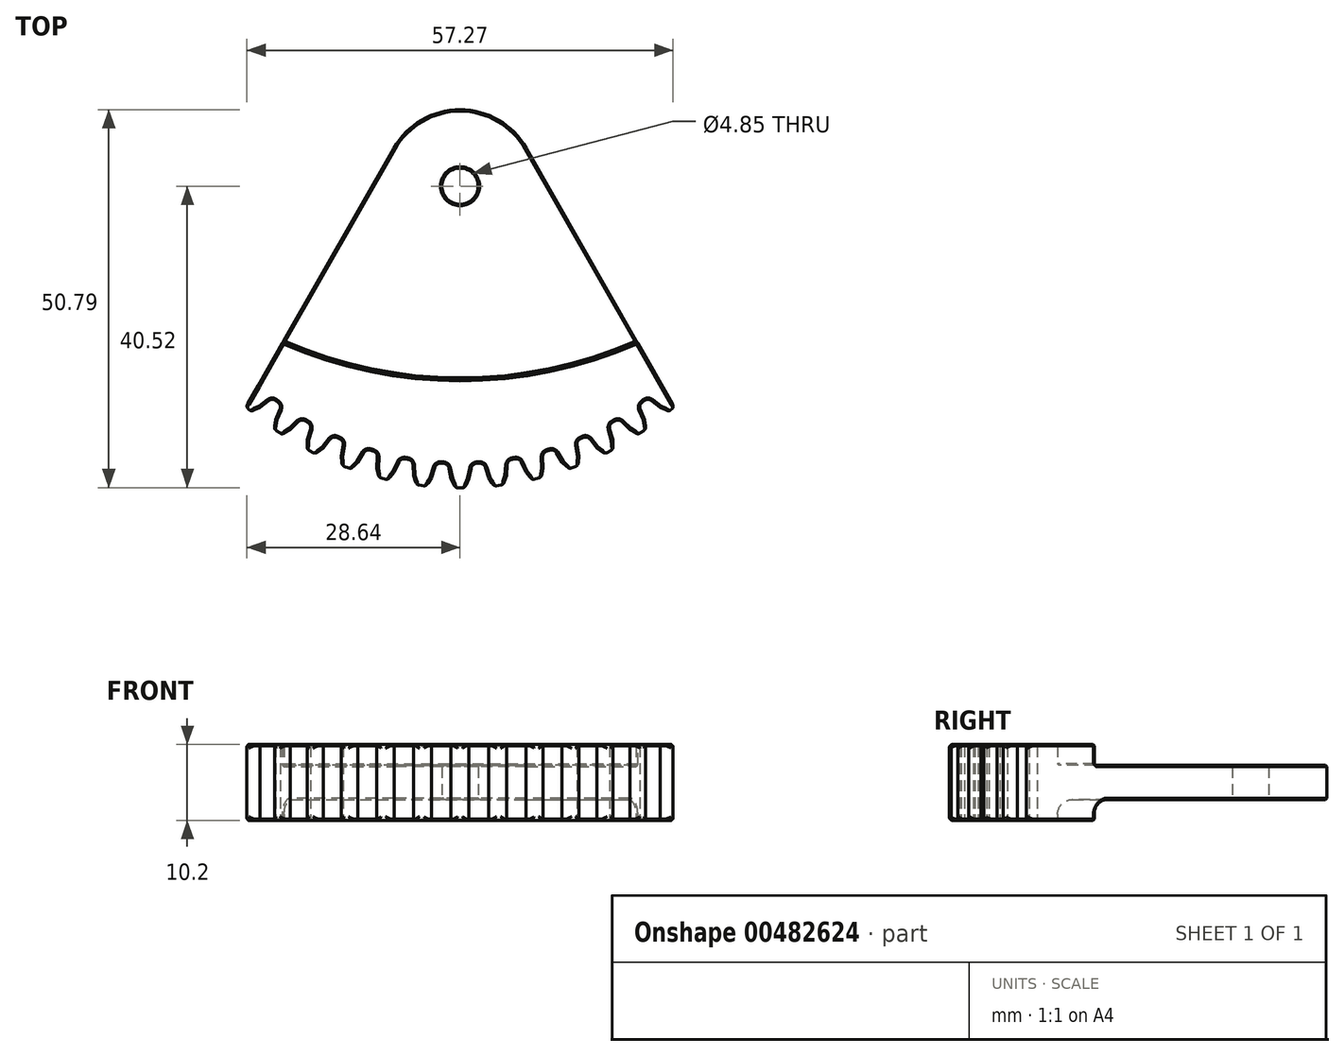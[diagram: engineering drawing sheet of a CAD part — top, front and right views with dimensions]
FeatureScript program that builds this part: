
annotation { "Feature Type Name" : "Feature", "Feature Type Description" : "" }
export const myFeature = defineFeature(function(context is Context, id is Id, definition is map)
    precondition{}
    {
        {
            var Q0;
            Q0=qCreatedBy(makeId("Top.planeOp"),FACE);
            var sketch = newSketch(context, id + "F0", { "sketchPlane" : qUnion([Q0])});
            skCircle(sketch, "E0", {"center": v(0, 0) * mm, "radius": 2.43 * mm});
            skCircle(sketch, "E1", {"center": v(0, 0) * mm, "radius": 10.27 * mm});
            skLineSegment(sketch, "E2", {"start": v(-8.92, 5.1) * mm, "end": v(-23.8, -20.96) * mm});
            skLineSegment(sketch, "E3.MirrorCS", {"start": v(8.92, 5.1) * mm, "end": v(23.8, -20.96) * mm});
            skLineSegment(sketch, "E4", {"start": v(-23.8, -20.96) * mm, "end": v(23.8, -20.96) * mm});
            skArc(sketch, "E5", {"start": v(-23.8, -20.96) * mm, "mid": v(0, -25.96) * mm, "end": v(23.8, -20.96) * mm});
            skArc(sketch, "E6", {"start": v(-27.15, -26.82) * mm, "mid": v(0, -37.32) * mm, "end": v(27.15, -26.82) * mm});
            skLineSegment(sketch, "E7", {"start": v(0, -25.96) * mm, "end": v(0, -37.32) * mm});
            skLineSegment(sketch, "E8", {"start": v(23.8, -20.96) * mm, "end": v(27.15, -26.82) * mm});
            skLineSegment(sketch, "E9", {"start": v(-23.8, -20.96) * mm, "end": v(-27.15, -26.82) * mm});
            skLineSegment(sketch, "E10", {"start": v(0, -37.32) * mm, "end": v(0, -40.52) * mm});
            skLineSegment(sketch, "E11", {"start": v(0, -40.52) * mm, "end": v(0.64, -40.52) * mm});
            skLineSegment(sketch, "E12", {"start": v(0.64, -40.52) * mm, "end": v(1.2, -39.35) * mm});
            skLineSegment(sketch, "E13", {"start": v(1.2, -39.35) * mm, "end": v(1.6, -37.28) * mm});
            skLineSegment(sketch, "E14.MirrorCS", {"start": v(-1.2, -39.35) * mm, "end": v(-1.6, -37.28) * mm});
            skLineSegment(sketch, "E15.MirrorCS", {"start": v(-0.64, -40.52) * mm, "end": v(-1.2, -39.35) * mm});
            skLineSegment(sketch, "E16.MirrorCS", {"start": v(0, -40.52) * mm, "end": v(-0.64, -40.52) * mm});
            skLineSegment(sketch, "E17.1.0", {"start": v(-3.85, -39.19) * mm, "end": v(-3.2, -37.19) * mm});
            skLineSegment(sketch, "E17.1.1", {"start": v(-6.23, -38.9) * mm, "end": v(-6.39, -36.8) * mm});
            skLineSegment(sketch, "E17.1.2", {"start": v(-5.82, -40.13) * mm, "end": v(-6.23, -38.9) * mm});
            skLineSegment(sketch, "E17.1.3", {"start": v(-5.18, -40.2) * mm, "end": v(-5.82, -40.13) * mm});
            skLineSegment(sketch, "E17.1.4", {"start": v(-5.18, -40.2) * mm, "end": v(-4.55, -40.28) * mm});
            skLineSegment(sketch, "E17.1.5", {"start": v(-4.55, -40.28) * mm, "end": v(-3.85, -39.19) * mm});
            skLineSegment(sketch, "E17.2.0", {"start": v(-8.85, -38.43) * mm, "end": v(-7.97, -36.52) * mm});
            skLineSegment(sketch, "E17.2.1", {"start": v(-11.18, -37.86) * mm, "end": v(-11.08, -35.76) * mm});
            skLineSegment(sketch, "E17.2.2", {"start": v(-10.91, -39.13) * mm, "end": v(-11.18, -37.86) * mm});
            skLineSegment(sketch, "E17.2.3", {"start": v(-10.29, -39.28) * mm, "end": v(-10.91, -39.13) * mm});
            skLineSegment(sketch, "E17.2.4", {"start": v(-10.29, -39.28) * mm, "end": v(-9.67, -39.43) * mm});
            skLineSegment(sketch, "E17.2.5", {"start": v(-9.67, -39.43) * mm, "end": v(-8.85, -38.43) * mm});
            skLineSegment(sketch, "E17.3.0", {"start": v(-13.72, -37.08) * mm, "end": v(-12.62, -35.3) * mm});
            skLineSegment(sketch, "E17.3.1", {"start": v(-15.97, -36.24) * mm, "end": v(-15.62, -34.17) * mm});
            skLineSegment(sketch, "E17.3.2", {"start": v(-15.85, -37.53) * mm, "end": v(-15.97, -36.24) * mm});
            skLineSegment(sketch, "E17.3.3", {"start": v(-15.25, -37.76) * mm, "end": v(-15.85, -37.53) * mm});
            skLineSegment(sketch, "E17.3.4", {"start": v(-15.25, -37.76) * mm, "end": v(-14.65, -37.98) * mm});
            skLineSegment(sketch, "E17.3.5", {"start": v(-14.65, -37.98) * mm, "end": v(-13.72, -37.08) * mm});
            skLineSegment(sketch, "E17.4.0", {"start": v(-18.4, -35.17) * mm, "end": v(-17.1, -33.52) * mm});
            skLineSegment(sketch, "E17.4.1", {"start": v(-20.53, -34.06) * mm, "end": v(-19.93, -32.05) * mm});
            skLineSegment(sketch, "E17.4.2", {"start": v(-20.57, -35.36) * mm, "end": v(-20.53, -34.06) * mm});
            skLineSegment(sketch, "E17.4.3", {"start": v(-20, -35.65) * mm, "end": v(-20.57, -35.36) * mm});
            skLineSegment(sketch, "E17.4.4", {"start": v(-20, -35.65) * mm, "end": v(-19.43, -35.95) * mm});
            skLineSegment(sketch, "E17.4.5", {"start": v(-19.43, -35.95) * mm, "end": v(-18.4, -35.17) * mm});
            skLineSegment(sketch, "E17.5.0", {"start": v(-22.8, -32.7) * mm, "end": v(-21.32, -31.22) * mm});
            skLineSegment(sketch, "E17.5.1", {"start": v(-24.8, -31.36) * mm, "end": v(-23.97, -29.43) * mm});
            skLineSegment(sketch, "E17.5.2", {"start": v(-24.99, -32.64) * mm, "end": v(-24.8, -31.36) * mm});
            skLineSegment(sketch, "E17.5.3", {"start": v(-24.46, -33) * mm, "end": v(-24.99, -32.64) * mm});
            skLineSegment(sketch, "E17.5.4", {"start": v(-24.46, -33) * mm, "end": v(-23.93, -33.36) * mm});
            skLineSegment(sketch, "E17.5.5", {"start": v(-23.93, -33.36) * mm, "end": v(-22.8, -32.7) * mm});
            skLineSegment(sketch, "E17.6.0", {"start": v(-26.9, -29.74) * mm, "end": v(-25.24, -28.44) * mm});
            skLineSegment(sketch, "E17.6.1", {"start": v(-28.7, -28.16) * mm, "end": v(-27.66, -26.34) * mm});
            skLineSegment(sketch, "E17.6.2", {"start": v(-29.05, -29.41) * mm, "end": v(-28.7, -28.16) * mm});
            skLineSegment(sketch, "E17.6.3", {"start": v(-28.57, -29.83) * mm, "end": v(-29.05, -29.41) * mm});
            skLineSegment(sketch, "E17.6.4", {"start": v(-28.57, -29.83) * mm, "end": v(-28.09, -30.25) * mm});
            skLineSegment(sketch, "E17.6.5", {"start": v(-28.09, -30.25) * mm, "end": v(-26.9, -29.74) * mm});
            skLineSegment(sketch, "E17.anchor1", {"start": v(0, 3.03) * mm, "end": v(1.2, -39.35) * mm, "construction": true});
            skLineSegment(sketch, "E17.anchor2", {"start": v(0, 3.03) * mm, "end": v(-26.9, -29.74) * mm, "construction": true});
            skLineSegment(sketch, "E18", {"start": v(-27.15, -26.82) * mm, "end": v(-28.78, -29.65) * mm});
            skLineSegment(sketch, "E19.1.0", {"start": v(6.23, -38.9) * mm, "end": v(6.39, -36.8) * mm});
            skLineSegment(sketch, "E19.1.1", {"start": v(5.82, -40.13) * mm, "end": v(6.23, -38.9) * mm});
            skLineSegment(sketch, "E19.1.2", {"start": v(5.18, -40.2) * mm, "end": v(5.82, -40.13) * mm});
            skLineSegment(sketch, "E19.1.3", {"start": v(5.18, -40.2) * mm, "end": v(4.55, -40.28) * mm});
            skLineSegment(sketch, "E19.1.4", {"start": v(4.55, -40.28) * mm, "end": v(3.85, -39.19) * mm});
            skLineSegment(sketch, "E19.1.5", {"start": v(3.85, -39.19) * mm, "end": v(3.2, -37.19) * mm});
            skLineSegment(sketch, "E19.2.0", {"start": v(11.18, -37.86) * mm, "end": v(11.08, -35.76) * mm});
            skLineSegment(sketch, "E19.2.1", {"start": v(10.91, -39.13) * mm, "end": v(11.18, -37.86) * mm});
            skLineSegment(sketch, "E19.2.2", {"start": v(10.29, -39.28) * mm, "end": v(10.91, -39.13) * mm});
            skLineSegment(sketch, "E19.2.3", {"start": v(10.29, -39.28) * mm, "end": v(9.67, -39.43) * mm});
            skLineSegment(sketch, "E19.2.4", {"start": v(9.67, -39.43) * mm, "end": v(8.85, -38.43) * mm});
            skLineSegment(sketch, "E19.2.5", {"start": v(8.85, -38.43) * mm, "end": v(7.97, -36.52) * mm});
            skLineSegment(sketch, "E19.3.0", {"start": v(15.97, -36.24) * mm, "end": v(15.62, -34.17) * mm});
            skLineSegment(sketch, "E19.3.1", {"start": v(15.85, -37.53) * mm, "end": v(15.97, -36.24) * mm});
            skLineSegment(sketch, "E19.3.2", {"start": v(15.25, -37.76) * mm, "end": v(15.85, -37.53) * mm});
            skLineSegment(sketch, "E19.3.3", {"start": v(15.25, -37.76) * mm, "end": v(14.65, -37.98) * mm});
            skLineSegment(sketch, "E19.3.4", {"start": v(14.65, -37.98) * mm, "end": v(13.72, -37.08) * mm});
            skLineSegment(sketch, "E19.3.5", {"start": v(13.72, -37.08) * mm, "end": v(12.62, -35.3) * mm});
            skLineSegment(sketch, "E19.4.0", {"start": v(20.53, -34.06) * mm, "end": v(19.93, -32.05) * mm});
            skLineSegment(sketch, "E19.4.1", {"start": v(20.57, -35.36) * mm, "end": v(20.53, -34.06) * mm});
            skLineSegment(sketch, "E19.4.2", {"start": v(20, -35.65) * mm, "end": v(20.57, -35.36) * mm});
            skLineSegment(sketch, "E19.4.3", {"start": v(20, -35.65) * mm, "end": v(19.43, -35.95) * mm});
            skLineSegment(sketch, "E19.4.4", {"start": v(19.43, -35.95) * mm, "end": v(18.4, -35.17) * mm});
            skLineSegment(sketch, "E19.4.5", {"start": v(18.4, -35.17) * mm, "end": v(17.1, -33.52) * mm});
            skLineSegment(sketch, "E19.5.0", {"start": v(24.8, -31.36) * mm, "end": v(23.97, -29.43) * mm});
            skLineSegment(sketch, "E19.5.1", {"start": v(24.99, -32.64) * mm, "end": v(24.8, -31.36) * mm});
            skLineSegment(sketch, "E19.5.2", {"start": v(24.46, -33) * mm, "end": v(24.99, -32.64) * mm});
            skLineSegment(sketch, "E19.5.3", {"start": v(24.46, -33) * mm, "end": v(23.93, -33.36) * mm});
            skLineSegment(sketch, "E19.5.4", {"start": v(23.93, -33.36) * mm, "end": v(22.8, -32.7) * mm});
            skLineSegment(sketch, "E19.5.5", {"start": v(22.8, -32.7) * mm, "end": v(21.32, -31.22) * mm});
            skLineSegment(sketch, "E19.6.0", {"start": v(28.7, -28.16) * mm, "end": v(27.66, -26.34) * mm});
            skLineSegment(sketch, "E19.6.1", {"start": v(29.05, -29.41) * mm, "end": v(28.7, -28.16) * mm});
            skLineSegment(sketch, "E19.6.2", {"start": v(28.57, -29.83) * mm, "end": v(29.05, -29.41) * mm});
            skLineSegment(sketch, "E19.6.3", {"start": v(28.57, -29.83) * mm, "end": v(28.09, -30.25) * mm});
            skLineSegment(sketch, "E19.6.4", {"start": v(28.09, -30.25) * mm, "end": v(26.9, -29.74) * mm});
            skLineSegment(sketch, "E19.6.5", {"start": v(26.9, -29.74) * mm, "end": v(25.24, -28.44) * mm});
            skLineSegment(sketch, "E19.anchor2", {"start": v(0, 3.03) * mm, "end": v(28.7, -28.16) * mm, "construction": true});
            skLineSegment(sketch, "E20", {"start": v(27.15, -26.82) * mm, "end": v(28.77, -29.66) * mm});
            skSolve(sketch);
        }
        {
            var Q0;
            {var subQ3=sQuery(id+"F0.wireOp",EDGE,"E17.6.0");Q0=makeQuery(id+"F0.imprint","IMPRINT",FACE,{"disambiguationData":[TD([[makeQuery(id+"F0.imprint","IMPRINT",EDGE,{"derivedFrom":subQ3}),1.0]])]});}
            var Q1;
            {var subQ1=sQuery(id+"F0.wireOp",EDGE,"E17.5.0");Q1=makeQuery(id+"F0.imprint","IMPRINT",FACE,{"disambiguationData":[TD([[makeQuery(id+"F0.imprint","IMPRINT",EDGE,{"derivedFrom":subQ1}),1.0]])]});}
            var Q2;
            {var subQ1=sQuery(id+"F0.wireOp",EDGE,"E17.4.0");Q2=makeQuery(id+"F0.imprint","IMPRINT",FACE,{"disambiguationData":[TD([[makeQuery(id+"F0.imprint","IMPRINT",EDGE,{"derivedFrom":subQ1}),1.0]])]});}
            var Q3;
            {var subQ0=sQuery(id+"F0.wireOp",EDGE,"E17.3.0");Q3=makeQuery(id+"F0.imprint","IMPRINT",FACE,{"disambiguationData":[TD([[makeQuery(id+"F0.imprint","IMPRINT",EDGE,{"derivedFrom":subQ0}),1.0]])]});}
            var Q4;
            {var subQ0=sQuery(id+"F0.wireOp",EDGE,"E17.2.0");Q4=makeQuery(id+"F0.imprint","IMPRINT",FACE,{"disambiguationData":[TD([[makeQuery(id+"F0.imprint","IMPRINT",EDGE,{"derivedFrom":subQ0}),1.0]])]});}
            var Q5;
            {var subQ1=sQuery(id+"F0.wireOp",EDGE,"E17.1.0");Q5=makeQuery(id+"F0.imprint","IMPRINT",FACE,{"disambiguationData":[TD([[makeQuery(id+"F0.imprint","IMPRINT",EDGE,{"derivedFrom":subQ1}),1.0]])]});}
            var Q6;
            {var subQ0=sQuery(id+"F0.wireOp",EDGE,"E19.1.0");Q6=makeQuery(id+"F0.imprint","IMPRINT",FACE,{"disambiguationData":[TD([[makeQuery(id+"F0.imprint","IMPRINT",EDGE,{"derivedFrom":subQ0}),1.0]])]});}
            var Q7;
            {var subQ0=sQuery(id+"F0.wireOp",EDGE,"E19.2.0");Q7=makeQuery(id+"F0.imprint","IMPRINT",FACE,{"disambiguationData":[TD([[makeQuery(id+"F0.imprint","IMPRINT",EDGE,{"derivedFrom":subQ0}),1.0]])]});}
            var Q8;
            {var subQ0=sQuery(id+"F0.wireOp",EDGE,"E19.3.0");Q8=makeQuery(id+"F0.imprint","IMPRINT",FACE,{"disambiguationData":[TD([[makeQuery(id+"F0.imprint","IMPRINT",EDGE,{"derivedFrom":subQ0}),1.0]])]});}
            var Q9;
            {var subQ0=sQuery(id+"F0.wireOp",EDGE,"E19.4.0");Q9=makeQuery(id+"F0.imprint","IMPRINT",FACE,{"disambiguationData":[TD([[makeQuery(id+"F0.imprint","IMPRINT",EDGE,{"derivedFrom":subQ0}),1.0]])]});}
            var Q10;
            {var subQ0=sQuery(id+"F0.wireOp",EDGE,"E19.5.0");Q10=makeQuery(id+"F0.imprint","IMPRINT",FACE,{"disambiguationData":[TD([[makeQuery(id+"F0.imprint","IMPRINT",EDGE,{"derivedFrom":subQ0}),1.0]])]});}
            var Q11;
            {var subQ0=sQuery(id+"F0.wireOp",EDGE,"E19.6.3");Q11=makeQuery(id+"F0.imprint","IMPRINT",FACE,{"disambiguationData":[TD([[makeQuery(id+"F0.imprint","IMPRINT",EDGE,{"derivedFrom":subQ0}),-1.0]])]});}
            var Q12;
            {var subQ1=sQuery(id+"F0.wireOp",EDGE,"E10");Q12=makeQuery(id+"F0.imprint","IMPRINT",FACE,{"disambiguationData":[TD([[makeQuery(id+"F0.imprint","IMPRINT",EDGE,{"derivedFrom":subQ1}),-1.0]])]});}
            var Q13;
            {var subQ0=sQuery(id+"F0.wireOp",EDGE,"E10");Q13=makeQuery(id+"F0.imprint","IMPRINT",FACE,{"disambiguationData":[TD([[makeQuery(id+"F0.imprint","IMPRINT",EDGE,{"derivedFrom":subQ0}),1.0]])]});}
            var Q14;
            {var subQ9=sQuery(id+"F0.wireOp",EDGE,"E7");Q14=makeQuery(id+"F0.imprint","IMPRINT",FACE,{"disambiguationData":[TD([[makeQuery(id+"F0.imprint","IMPRINT",EDGE,{"derivedFrom":subQ9}),-1.0]])]});}
            var Q15;
            {var subQ10=sQuery(id+"F0.wireOp",EDGE,"E7");Q15=makeQuery(id+"F0.imprint","IMPRINT",FACE,{"disambiguationData":[TD([[makeQuery(id+"F0.imprint","IMPRINT",EDGE,{"derivedFrom":subQ10}),1.0]])]});}
            extrude(context, id + "F1", {"entities" : qUnion([Q0, Q1, Q2, Q3, Q4, Q5, Q6, Q7, Q8, Q9, Q10, Q11, Q12, Q13, Q14, Q15]), "depth" : 5.1 * mm, "hasSecondDirection" : true, "secondDirectionOppositeDirection" : true, "secondDirectionDepth" : 5.1 * mm, "offsetDistance" : 25 * mm});
        }
        {
            var Q0;
            {var subQ0=sQuery(id+"F0.wireOp",EDGE,"E2");Q0=makeQuery(id+"F0.imprint","IMPRINT",FACE,{"disambiguationData":[TD([[makeQuery(id+"F0.imprint","IMPRINT",EDGE,{"derivedFrom":subQ0}),1.0]])]});}
            var Q1;
            Q1=makeQuery(id+"F0.imprint","IMPRINT",FACE,{"disambiguationData":[TD([[makeQuery(id+"F0.imprint","IMPRINT",EDGE,{"derivedFrom":sQuery(id+"F0.wireOp",EDGE,"E0")}),-1.0]])]});
            var Q2;
            {var subQ0=sQuery(id+"F0.wireOp",EDGE,"E4");Q2=makeQuery(id+"F0.imprint","IMPRINT",FACE,{"disambiguationData":[TD([[makeQuery(id+"F0.imprint","IMPRINT",EDGE,{"derivedFrom":subQ0}),-1.0]])]});}
            extrude(context, id + "F2", {"entities" : qUnion([Q0, Q1, Q2]), "operationType" : NewBodyOperationType.ADD, "depth" : 2.3 * mm, "hasSecondDirection" : true, "secondDirectionOppositeDirection" : true, "secondDirectionDepth" : 2.3 * mm});
        }
        {
            var Q0;
            Q0=makeQuery(id+"F2.opExtrude","CAP_EDGE",EDGE,{"disambiguationData":[OSD([sQuery(id+"F0.wireOp",EDGE,"E5")])],"isStart":false});
            var Q1;
            Q1=makeQuery(id+"F2.opExtrude","CAP_EDGE",EDGE,{"disambiguationData":[OSD([sQuery(id+"F0.wireOp",EDGE,"E5")])],"isStart":true});
            fillet(context, id + "F3", {"entities" : qUnion([Q0, Q1]), "radius" : 2 * mm, "tangentPropagation" : true, "allowEdgeOverflow" : false});
        }
        {
            var Q0;
            Q0=makeQuery(id+"F1.opExtrude","SWEPT_FACE",FACE,{"disambiguationData":[OSD([sQuery(id+"F0.wireOp",EDGE,"E17.6.3"),sQuery(id+"F0.wireOp",EDGE,"E17.6.4")])]});
            var Q1;
            Q1=makeQuery(id+"F1.opExtrude","SWEPT_FACE",FACE,{"disambiguationData":[OSD([sQuery(id+"F0.wireOp",EDGE,"E17.5.3"),sQuery(id+"F0.wireOp",EDGE,"E17.5.4")])]});
            var Q2;
            Q2=makeQuery(id+"F1.opExtrude","SWEPT_FACE",FACE,{"disambiguationData":[OSD([sQuery(id+"F0.wireOp",EDGE,"E17.4.3"),sQuery(id+"F0.wireOp",EDGE,"E17.4.4")])]});
            var Q3;
            Q3=makeQuery(id+"F1.opExtrude","SWEPT_FACE",FACE,{"disambiguationData":[OSD([sQuery(id+"F0.wireOp",EDGE,"E17.3.3"),sQuery(id+"F0.wireOp",EDGE,"E17.3.4")])]});
            var Q4;
            Q4=makeQuery(id+"F1.opExtrude","SWEPT_FACE",FACE,{"disambiguationData":[OSD([sQuery(id+"F0.wireOp",EDGE,"E17.2.3"),sQuery(id+"F0.wireOp",EDGE,"E17.2.4")])]});
            var Q5;
            Q5=makeQuery(id+"F1.opExtrude","SWEPT_FACE",FACE,{"disambiguationData":[OSD([sQuery(id+"F0.wireOp",EDGE,"E17.1.3"),sQuery(id+"F0.wireOp",EDGE,"E17.1.4")])]});
            var Q6;
            Q6=makeQuery(id+"F1.opExtrude","SWEPT_FACE",FACE,{"disambiguationData":[OSD([sQuery(id+"F0.wireOp",EDGE,"E11"),sQuery(id+"F0.wireOp",EDGE,"E16.MirrorCS")])]});
            var Q7;
            Q7=makeQuery(id+"F1.opExtrude","SWEPT_FACE",FACE,{"disambiguationData":[OSD([sQuery(id+"F0.wireOp",EDGE,"E19.1.2"),sQuery(id+"F0.wireOp",EDGE,"E19.1.3")])]});
            var Q8;
            Q8=makeQuery(id+"F1.opExtrude","SWEPT_FACE",FACE,{"disambiguationData":[OSD([sQuery(id+"F0.wireOp",EDGE,"E19.2.2"),sQuery(id+"F0.wireOp",EDGE,"E19.2.3")])]});
            var Q9;
            Q9=makeQuery(id+"F1.opExtrude","SWEPT_FACE",FACE,{"disambiguationData":[OSD([sQuery(id+"F0.wireOp",EDGE,"E19.3.2"),sQuery(id+"F0.wireOp",EDGE,"E19.3.3")])]});
            var Q10;
            Q10=makeQuery(id+"F1.opExtrude","SWEPT_FACE",FACE,{"disambiguationData":[OSD([sQuery(id+"F0.wireOp",EDGE,"E19.4.2"),sQuery(id+"F0.wireOp",EDGE,"E19.4.3")])]});
            var Q11;
            Q11=makeQuery(id+"F1.opExtrude","SWEPT_FACE",FACE,{"disambiguationData":[OSD([sQuery(id+"F0.wireOp",EDGE,"E19.5.2"),sQuery(id+"F0.wireOp",EDGE,"E19.5.3")])]});
            var Q12;
            Q12=makeQuery(id+"F1.opExtrude","SWEPT_FACE",FACE,{"disambiguationData":[OSD([sQuery(id+"F0.wireOp",EDGE,"E19.6.2"),sQuery(id+"F0.wireOp",EDGE,"E19.6.3")])]});
            fillet(context, id + "F4", {"entities" : qUnion([Q0, Q1, Q2, Q3, Q4, Q5, Q6, Q7, Q8, Q9, Q10, Q11, Q12]), "radius" : .5 * mm, "tangentPropagation" : true, "allowEdgeOverflow" : false});
        }
        {
            var Q0;
            Q0=makeQuery(id+"F1.opExtrude","SWEPT_EDGE",EDGE,{"disambiguationData":[OSD([sQuery(id+"F0.wireOp",EDGE,"E6"),sQuery(id+"F0.wireOp",EDGE,"E19.6.5")])]});
            var Q1;
            Q1=makeQuery(id+"F1.opExtrude","SWEPT_EDGE",EDGE,{"disambiguationData":[OSD([sQuery(id+"F0.wireOp",EDGE,"E6"),sQuery(id+"F0.wireOp",EDGE,"E19.4.0")])]});
            var Q2;
            Q2=makeQuery(id+"F1.opExtrude","SWEPT_EDGE",EDGE,{"disambiguationData":[OSD([sQuery(id+"F0.wireOp",EDGE,"E6"),sQuery(id+"F0.wireOp",EDGE,"E19.5.0")])]});
            var Q3;
            Q3=makeQuery(id+"F1.opExtrude","SWEPT_EDGE",EDGE,{"disambiguationData":[OSD([sQuery(id+"F0.wireOp",EDGE,"E6"),sQuery(id+"F0.wireOp",EDGE,"E19.5.5")])]});
            var Q4;
            Q4=makeQuery(id+"F1.opExtrude","SWEPT_EDGE",EDGE,{"disambiguationData":[OSD([sQuery(id+"F0.wireOp",EDGE,"E6"),sQuery(id+"F0.wireOp",EDGE,"E19.4.5")])]});
            var Q5;
            Q5=makeQuery(id+"F1.opExtrude","SWEPT_EDGE",EDGE,{"disambiguationData":[OSD([sQuery(id+"F0.wireOp",EDGE,"E6"),sQuery(id+"F0.wireOp",EDGE,"E19.3.0")])]});
            var Q6;
            Q6=makeQuery(id+"F1.opExtrude","SWEPT_EDGE",EDGE,{"disambiguationData":[OSD([sQuery(id+"F0.wireOp",EDGE,"E6"),sQuery(id+"F0.wireOp",EDGE,"E19.3.5")])]});
            var Q7;
            Q7=makeQuery(id+"F1.opExtrude","SWEPT_EDGE",EDGE,{"disambiguationData":[OSD([sQuery(id+"F0.wireOp",EDGE,"E6"),sQuery(id+"F0.wireOp",EDGE,"E19.2.0")])]});
            var Q8;
            Q8=makeQuery(id+"F1.opExtrude","SWEPT_EDGE",EDGE,{"disambiguationData":[OSD([sQuery(id+"F0.wireOp",EDGE,"E6"),sQuery(id+"F0.wireOp",EDGE,"E19.2.5")])]});
            var Q9;
            Q9=makeQuery(id+"F1.opExtrude","SWEPT_EDGE",EDGE,{"disambiguationData":[OSD([sQuery(id+"F0.wireOp",EDGE,"E6"),sQuery(id+"F0.wireOp",EDGE,"E19.1.0")])]});
            var Q10;
            Q10=makeQuery(id+"F1.opExtrude","SWEPT_EDGE",EDGE,{"disambiguationData":[OSD([sQuery(id+"F0.wireOp",EDGE,"E6"),sQuery(id+"F0.wireOp",EDGE,"E19.1.5")])]});
            var Q11;
            Q11=makeQuery(id+"F1.opExtrude","SWEPT_EDGE",EDGE,{"disambiguationData":[OSD([sQuery(id+"F0.wireOp",EDGE,"E6"),sQuery(id+"F0.wireOp",EDGE,"E13")])]});
            var Q12;
            Q12=makeQuery(id+"F1.opExtrude","SWEPT_EDGE",EDGE,{"disambiguationData":[OSD([sQuery(id+"F0.wireOp",EDGE,"E6"),sQuery(id+"F0.wireOp",EDGE,"E14.MirrorCS")])]});
            var Q13;
            Q13=makeQuery(id+"F1.opExtrude","SWEPT_EDGE",EDGE,{"disambiguationData":[OSD([sQuery(id+"F0.wireOp",EDGE,"E6"),sQuery(id+"F0.wireOp",EDGE,"E17.1.0")])]});
            var Q14;
            Q14=makeQuery(id+"F1.opExtrude","SWEPT_EDGE",EDGE,{"disambiguationData":[OSD([sQuery(id+"F0.wireOp",EDGE,"E6"),sQuery(id+"F0.wireOp",EDGE,"E17.1.1")])]});
            var Q15;
            Q15=makeQuery(id+"F1.opExtrude","SWEPT_EDGE",EDGE,{"disambiguationData":[OSD([sQuery(id+"F0.wireOp",EDGE,"E6"),sQuery(id+"F0.wireOp",EDGE,"E17.2.0")])]});
            var Q16;
            Q16=makeQuery(id+"F1.opExtrude","SWEPT_EDGE",EDGE,{"disambiguationData":[OSD([sQuery(id+"F0.wireOp",EDGE,"E6"),sQuery(id+"F0.wireOp",EDGE,"E17.2.1")])]});
            var Q17;
            Q17=makeQuery(id+"F1.opExtrude","SWEPT_EDGE",EDGE,{"disambiguationData":[OSD([sQuery(id+"F0.wireOp",EDGE,"E6"),sQuery(id+"F0.wireOp",EDGE,"E17.3.0")])]});
            var Q18;
            Q18=makeQuery(id+"F1.opExtrude","SWEPT_EDGE",EDGE,{"disambiguationData":[OSD([sQuery(id+"F0.wireOp",EDGE,"E6"),sQuery(id+"F0.wireOp",EDGE,"E17.3.1")])]});
            var Q19;
            Q19=makeQuery(id+"F1.opExtrude","SWEPT_EDGE",EDGE,{"disambiguationData":[OSD([sQuery(id+"F0.wireOp",EDGE,"E6"),sQuery(id+"F0.wireOp",EDGE,"E17.4.0")])]});
            var Q20;
            Q20=makeQuery(id+"F1.opExtrude","SWEPT_EDGE",EDGE,{"disambiguationData":[OSD([sQuery(id+"F0.wireOp",EDGE,"E6"),sQuery(id+"F0.wireOp",EDGE,"E17.5.0")])]});
            var Q21;
            Q21=makeQuery(id+"F1.opExtrude","SWEPT_EDGE",EDGE,{"disambiguationData":[OSD([sQuery(id+"F0.wireOp",EDGE,"E6"),sQuery(id+"F0.wireOp",EDGE,"E17.4.1")])]});
            var Q22;
            Q22=makeQuery(id+"F1.opExtrude","SWEPT_EDGE",EDGE,{"disambiguationData":[OSD([sQuery(id+"F0.wireOp",EDGE,"E6"),sQuery(id+"F0.wireOp",EDGE,"E17.5.1")])]});
            var Q23;
            Q23=makeQuery(id+"F1.opExtrude","SWEPT_EDGE",EDGE,{"disambiguationData":[OSD([sQuery(id+"F0.wireOp",EDGE,"E6"),sQuery(id+"F0.wireOp",EDGE,"E17.6.0")])]});
            fillet(context, id + "F5", {"entities" : qUnion([Q0, Q1, Q2, Q3, Q4, Q5, Q6, Q7, Q8, Q9, Q10, Q11, Q12, Q13, Q14, Q15, Q16, Q17, Q18, Q19, Q20, Q21, Q22, Q23]), "radius" : .8 * mm, "tangentPropagation" : true, "allowEdgeOverflow" : false});
        }
        {
            var Q0;
            Q0=makeQuery(id+"F1.opExtrude","CAP_FACE",FACE,{"disambiguationData":[OSD([sQuery(id+"F0.wireOp",EDGE,"E5"),sQuery(id+"F0.wireOp",EDGE,"E6"),sQuery(id+"F0.wireOp",EDGE,"E8"),sQuery(id+"F0.wireOp",EDGE,"E9"),sQuery(id+"F0.wireOp",EDGE,"E11"),sQuery(id+"F0.wireOp",EDGE,"E12"),sQuery(id+"F0.wireOp",EDGE,"E13"),sQuery(id+"F0.wireOp",EDGE,"E14.MirrorCS"),sQuery(id+"F0.wireOp",EDGE,"E15.MirrorCS"),sQuery(id+"F0.wireOp",EDGE,"E16.MirrorCS"),sQuery(id+"F0.wireOp",EDGE,"E17.1.0"),sQuery(id+"F0.wireOp",EDGE,"E17.1.1"),sQuery(id+"F0.wireOp",EDGE,"E17.1.2"),sQuery(id+"F0.wireOp",EDGE,"E17.1.3"),sQuery(id+"F0.wireOp",EDGE,"E17.1.4"),sQuery(id+"F0.wireOp",EDGE,"E17.1.5"),sQuery(id+"F0.wireOp",EDGE,"E17.2.0"),sQuery(id+"F0.wireOp",EDGE,"E17.2.1"),sQuery(id+"F0.wireOp",EDGE,"E17.2.2"),sQuery(id+"F0.wireOp",EDGE,"E17.2.3"),sQuery(id+"F0.wireOp",EDGE,"E17.2.4"),sQuery(id+"F0.wireOp",EDGE,"E17.2.5"),sQuery(id+"F0.wireOp",EDGE,"E17.3.0"),sQuery(id+"F0.wireOp",EDGE,"E17.3.1"),sQuery(id+"F0.wireOp",EDGE,"E17.3.2"),sQuery(id+"F0.wireOp",EDGE,"E17.3.3"),sQuery(id+"F0.wireOp",EDGE,"E17.3.4"),sQuery(id+"F0.wireOp",EDGE,"E17.3.5"),sQuery(id+"F0.wireOp",EDGE,"E17.4.0"),sQuery(id+"F0.wireOp",EDGE,"E17.4.1"),sQuery(id+"F0.wireOp",EDGE,"E17.4.2"),sQuery(id+"F0.wireOp",EDGE,"E17.4.3"),sQuery(id+"F0.wireOp",EDGE,"E17.4.4"),sQuery(id+"F0.wireOp",EDGE,"E17.4.5"),sQuery(id+"F0.wireOp",EDGE,"E17.5.0"),sQuery(id+"F0.wireOp",EDGE,"E17.5.1"),sQuery(id+"F0.wireOp",EDGE,"E17.5.2"),sQuery(id+"F0.wireOp",EDGE,"E17.5.3"),sQuery(id+"F0.wireOp",EDGE,"E17.5.4"),sQuery(id+"F0.wireOp",EDGE,"E17.5.5"),sQuery(id+"F0.wireOp",EDGE,"E17.6.0"),sQuery(id+"F0.wireOp",EDGE,"E17.6.3"),sQuery(id+"F0.wireOp",EDGE,"E17.6.4"),sQuery(id+"F0.wireOp",EDGE,"E17.6.5"),sQuery(id+"F0.wireOp",EDGE,"E18"),sQuery(id+"F0.wireOp",EDGE,"E19.1.0"),sQuery(id+"F0.wireOp",EDGE,"E19.1.1"),sQuery(id+"F0.wireOp",EDGE,"E19.1.2"),sQuery(id+"F0.wireOp",EDGE,"E19.1.3"),sQuery(id+"F0.wireOp",EDGE,"E19.1.4"),sQuery(id+"F0.wireOp",EDGE,"E19.1.5"),sQuery(id+"F0.wireOp",EDGE,"E19.2.0"),sQuery(id+"F0.wireOp",EDGE,"E19.2.1"),sQuery(id+"F0.wireOp",EDGE,"E19.2.2"),sQuery(id+"F0.wireOp",EDGE,"E19.2.3"),sQuery(id+"F0.wireOp",EDGE,"E19.2.4"),sQuery(id+"F0.wireOp",EDGE,"E19.2.5"),sQuery(id+"F0.wireOp",EDGE,"E19.3.0"),sQuery(id+"F0.wireOp",EDGE,"E19.3.1"),sQuery(id+"F0.wireOp",EDGE,"E19.3.2"),sQuery(id+"F0.wireOp",EDGE,"E19.3.3"),sQuery(id+"F0.wireOp",EDGE,"E19.3.4"),sQuery(id+"F0.wireOp",EDGE,"E19.3.5"),sQuery(id+"F0.wireOp",EDGE,"E19.4.0"),sQuery(id+"F0.wireOp",EDGE,"E19.4.1"),sQuery(id+"F0.wireOp",EDGE,"E19.4.2"),sQuery(id+"F0.wireOp",EDGE,"E19.4.3"),sQuery(id+"F0.wireOp",EDGE,"E19.4.4"),sQuery(id+"F0.wireOp",EDGE,"E19.4.5"),sQuery(id+"F0.wireOp",EDGE,"E19.5.0"),sQuery(id+"F0.wireOp",EDGE,"E19.5.1"),sQuery(id+"F0.wireOp",EDGE,"E19.5.2"),sQuery(id+"F0.wireOp",EDGE,"E19.5.3"),sQuery(id+"F0.wireOp",EDGE,"E19.5.4"),sQuery(id+"F0.wireOp",EDGE,"E19.5.5"),sQuery(id+"F0.wireOp",EDGE,"E19.6.2"),sQuery(id+"F0.wireOp",EDGE,"E19.6.3"),sQuery(id+"F0.wireOp",EDGE,"E19.6.4"),sQuery(id+"F0.wireOp",EDGE,"E19.6.5"),sQuery(id+"F0.wireOp",EDGE,"E20")])],"isStart":false});
            var Q1;
            Q1=makeQuery(id+"F1.opExtrude","CAP_FACE",FACE,{"disambiguationData":[OSD([sQuery(id+"F0.wireOp",EDGE,"E5"),sQuery(id+"F0.wireOp",EDGE,"E6"),sQuery(id+"F0.wireOp",EDGE,"E8"),sQuery(id+"F0.wireOp",EDGE,"E9"),sQuery(id+"F0.wireOp",EDGE,"E11"),sQuery(id+"F0.wireOp",EDGE,"E12"),sQuery(id+"F0.wireOp",EDGE,"E13"),sQuery(id+"F0.wireOp",EDGE,"E14.MirrorCS"),sQuery(id+"F0.wireOp",EDGE,"E15.MirrorCS"),sQuery(id+"F0.wireOp",EDGE,"E16.MirrorCS"),sQuery(id+"F0.wireOp",EDGE,"E17.1.0"),sQuery(id+"F0.wireOp",EDGE,"E17.1.1"),sQuery(id+"F0.wireOp",EDGE,"E17.1.2"),sQuery(id+"F0.wireOp",EDGE,"E17.1.3"),sQuery(id+"F0.wireOp",EDGE,"E17.1.4"),sQuery(id+"F0.wireOp",EDGE,"E17.1.5"),sQuery(id+"F0.wireOp",EDGE,"E17.2.0"),sQuery(id+"F0.wireOp",EDGE,"E17.2.1"),sQuery(id+"F0.wireOp",EDGE,"E17.2.2"),sQuery(id+"F0.wireOp",EDGE,"E17.2.3"),sQuery(id+"F0.wireOp",EDGE,"E17.2.4"),sQuery(id+"F0.wireOp",EDGE,"E17.2.5"),sQuery(id+"F0.wireOp",EDGE,"E17.3.0"),sQuery(id+"F0.wireOp",EDGE,"E17.3.1"),sQuery(id+"F0.wireOp",EDGE,"E17.3.2"),sQuery(id+"F0.wireOp",EDGE,"E17.3.3"),sQuery(id+"F0.wireOp",EDGE,"E17.3.4"),sQuery(id+"F0.wireOp",EDGE,"E17.3.5"),sQuery(id+"F0.wireOp",EDGE,"E17.4.0"),sQuery(id+"F0.wireOp",EDGE,"E17.4.1"),sQuery(id+"F0.wireOp",EDGE,"E17.4.2"),sQuery(id+"F0.wireOp",EDGE,"E17.4.3"),sQuery(id+"F0.wireOp",EDGE,"E17.4.4"),sQuery(id+"F0.wireOp",EDGE,"E17.4.5"),sQuery(id+"F0.wireOp",EDGE,"E17.5.0"),sQuery(id+"F0.wireOp",EDGE,"E17.5.1"),sQuery(id+"F0.wireOp",EDGE,"E17.5.2"),sQuery(id+"F0.wireOp",EDGE,"E17.5.3"),sQuery(id+"F0.wireOp",EDGE,"E17.5.4"),sQuery(id+"F0.wireOp",EDGE,"E17.5.5"),sQuery(id+"F0.wireOp",EDGE,"E17.6.0"),sQuery(id+"F0.wireOp",EDGE,"E17.6.3"),sQuery(id+"F0.wireOp",EDGE,"E17.6.4"),sQuery(id+"F0.wireOp",EDGE,"E17.6.5"),sQuery(id+"F0.wireOp",EDGE,"E18"),sQuery(id+"F0.wireOp",EDGE,"E19.1.0"),sQuery(id+"F0.wireOp",EDGE,"E19.1.1"),sQuery(id+"F0.wireOp",EDGE,"E19.1.2"),sQuery(id+"F0.wireOp",EDGE,"E19.1.3"),sQuery(id+"F0.wireOp",EDGE,"E19.1.4"),sQuery(id+"F0.wireOp",EDGE,"E19.1.5"),sQuery(id+"F0.wireOp",EDGE,"E19.2.0"),sQuery(id+"F0.wireOp",EDGE,"E19.2.1"),sQuery(id+"F0.wireOp",EDGE,"E19.2.2"),sQuery(id+"F0.wireOp",EDGE,"E19.2.3"),sQuery(id+"F0.wireOp",EDGE,"E19.2.4"),sQuery(id+"F0.wireOp",EDGE,"E19.2.5"),sQuery(id+"F0.wireOp",EDGE,"E19.3.0"),sQuery(id+"F0.wireOp",EDGE,"E19.3.1"),sQuery(id+"F0.wireOp",EDGE,"E19.3.2"),sQuery(id+"F0.wireOp",EDGE,"E19.3.3"),sQuery(id+"F0.wireOp",EDGE,"E19.3.4"),sQuery(id+"F0.wireOp",EDGE,"E19.3.5"),sQuery(id+"F0.wireOp",EDGE,"E19.4.0"),sQuery(id+"F0.wireOp",EDGE,"E19.4.1"),sQuery(id+"F0.wireOp",EDGE,"E19.4.2"),sQuery(id+"F0.wireOp",EDGE,"E19.4.3"),sQuery(id+"F0.wireOp",EDGE,"E19.4.4"),sQuery(id+"F0.wireOp",EDGE,"E19.4.5"),sQuery(id+"F0.wireOp",EDGE,"E19.5.0"),sQuery(id+"F0.wireOp",EDGE,"E19.5.1"),sQuery(id+"F0.wireOp",EDGE,"E19.5.2"),sQuery(id+"F0.wireOp",EDGE,"E19.5.3"),sQuery(id+"F0.wireOp",EDGE,"E19.5.4"),sQuery(id+"F0.wireOp",EDGE,"E19.5.5"),sQuery(id+"F0.wireOp",EDGE,"E19.6.2"),sQuery(id+"F0.wireOp",EDGE,"E19.6.3"),sQuery(id+"F0.wireOp",EDGE,"E19.6.4"),sQuery(id+"F0.wireOp",EDGE,"E19.6.5"),sQuery(id+"F0.wireOp",EDGE,"E20")])],"isStart":true});
            var Q2;
            Q2=makeQuery(id+"F2.opExtrude","CAP_FACE",FACE,{"disambiguationData":[OSD([sQuery(id+"F0.wireOp",EDGE,"E0"),sQuery(id+"F0.wireOp",EDGE,"E1"),sQuery(id+"F0.wireOp",EDGE,"E2"),sQuery(id+"F0.wireOp",EDGE,"E3.MirrorCS"),sQuery(id+"F0.wireOp",EDGE,"E5")])],"isStart":false});
            var Q3;
            Q3=makeQuery(id+"F2.opExtrude","CAP_FACE",FACE,{"disambiguationData":[OSD([sQuery(id+"F0.wireOp",EDGE,"E0"),sQuery(id+"F0.wireOp",EDGE,"E1"),sQuery(id+"F0.wireOp",EDGE,"E2"),sQuery(id+"F0.wireOp",EDGE,"E3.MirrorCS"),sQuery(id+"F0.wireOp",EDGE,"E5")])],"isStart":true});
            chamfer(context, id + "F6", {"entities" : qUnion([Q0, Q1, Q2, Q3]), "width" : .2 * mm, "tangentPropagation" : true});
        }
    });
